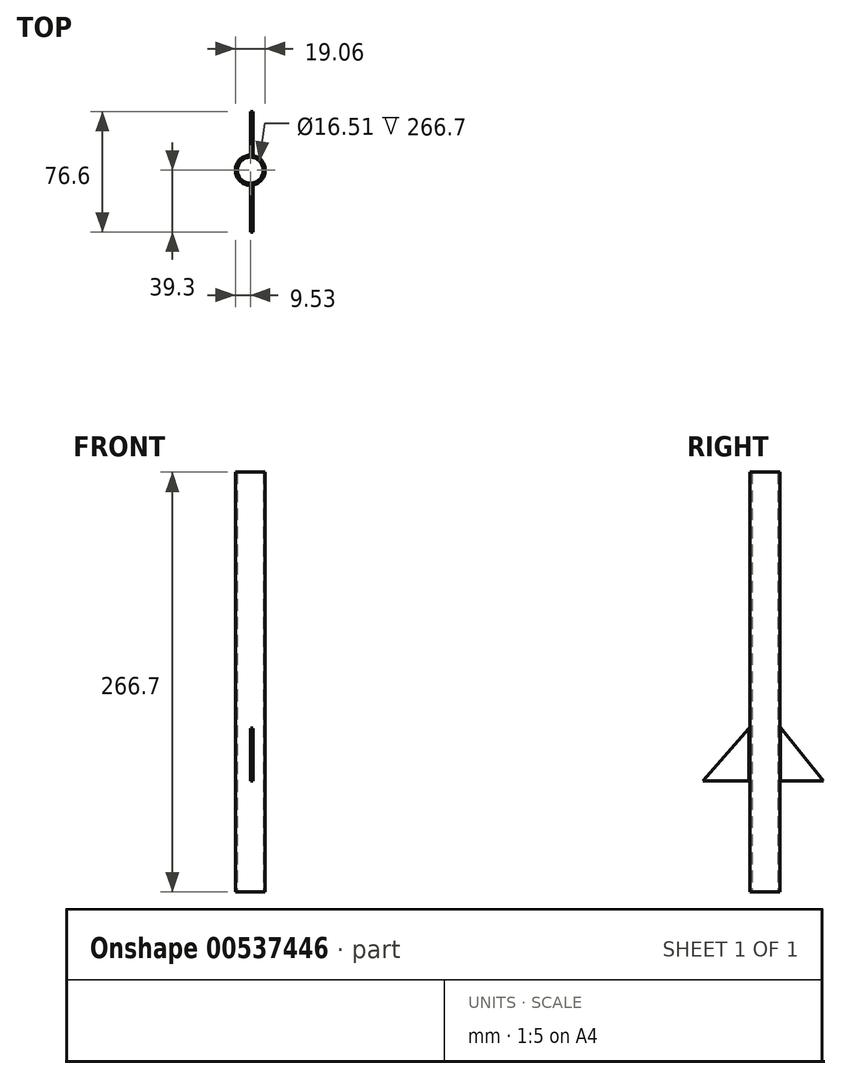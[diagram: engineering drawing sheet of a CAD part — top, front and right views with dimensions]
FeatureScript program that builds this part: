
annotation { "Feature Type Name" : "Feature", "Feature Type Description" : "" }
export const myFeature = defineFeature(function(context is Context, id is Id, definition is map)
    precondition{}
    {
        {
            var Q0;
            Q0=qCreatedBy(makeId("Top.planeOp"),FACE);
            var sketch = newSketch(context, id + "F0", { "sketchPlane" : qUnion([Q0])});
            skCircle(sketch, "E0", {"center": v(0, 0) * mm, "radius": 9.53 * mm});
            skCircle(sketch, "E1", {"center": v(0, 0) * mm, "radius": 8.26 * mm});
            skSolve(sketch);
        }
        {
            var Q0;
            Q0=makeQuery(id+"F0.imprint","IMPRINT",FACE,{"disambiguationData":[TD([[makeQuery(id+"F0.imprint","IMPRINT",EDGE,{"derivedFrom":sQuery(id+"F0.wireOp",EDGE,"E0")}),1.0]])]});
            extrude(context, id + "F1", {"entities" : qUnion([Q0]), "endBound" : BoundingType.SYMMETRIC, "depth" : 266.7 * mm, "offsetDistance" : 25.4 * mm});
        }
        {
            var Q0;
            Q0=qCreatedBy(makeId("Right.planeOp"),FACE);
            var sketch = newSketch(context, id + "F2", { "sketchPlane" : qUnion([Q0])});
            skLineSegment(sketch, "E2", {"start": v(9.93, -62.87) * mm, "end": v(9.93, -28.88) * mm});
            skLineSegment(sketch, "E3", {"start": v(9.93, -28.88) * mm, "end": v(37.3, -62.87) * mm});
            skLineSegment(sketch, "E4", {"start": v(37.3, -62.87) * mm, "end": v(9.93, -62.87) * mm});
            skSolve(sketch);
        }
        {
            var Q0;
            Q0=qCreatedBy(makeId("Right.planeOp"),FACE);
            var sketch = newSketch(context, id + "F3", { "sketchPlane" : qUnion([Q0])});
            skLineSegment(sketch, "E5", {"start": v(10.1, -62.89) * mm, "end": v(-39.3, -62.89) * mm});
            skLineSegment(sketch, "E6", {"start": v(-39.3, -62.89) * mm, "end": v(-10.1, -29.48) * mm});
            skLineSegment(sketch, "E7", {"start": v(-10.1, -29.48) * mm, "end": v(-10.1, -62.89) * mm});
            skLineSegment(sketch, "E8", {"start": v(-10.1, -62.89) * mm, "end": v(-10.1, -29.48) * mm});
            skLineSegment(sketch, "E9", {"start": v(10.39, -29.48) * mm, "end": v(-10.1, -29.48) * mm});
            skLineSegment(sketch, "E10", {"start": v(10.1, -62.89) * mm, "end": v(10.39, -29.48) * mm});
            skLineSegment(sketch, "E11", {"start": v(37.62, -62.89) * mm, "end": v(10.39, -29.48) * mm});
            skLineSegment(sketch, "E12", {"start": v(10.1, -62.89) * mm, "end": v(37.62, -62.89) * mm});
            skSolve(sketch);
        }
        {
            var Q0;
            Q0=makeQuery(id+"F2.imprint","IMPRINT",FACE,{"disambiguationData":[TD([[makeQuery(id+"F2.imprint","IMPRINT",EDGE,{"derivedFrom":sQuery(id+"F2.wireOp",EDGE,"E2")}),-1.0]])]});
            var Q1;
            {var subQ0=sQuery(id+"F3.wireOp",EDGE,"E6");Q1=makeQuery(id+"F3.imprint","IMPRINT",FACE,{"disambiguationData":[TD([[makeQuery(id+"F3.imprint","IMPRINT",EDGE,{"derivedFrom":subQ0}),-1.0]])]});}
            extrude(context, id + "F4", {"entities" : qUnion([Q0, Q1]), "depth" : 1.78 * mm, "offsetDistance" : 25.4 * mm});
        }
    });
